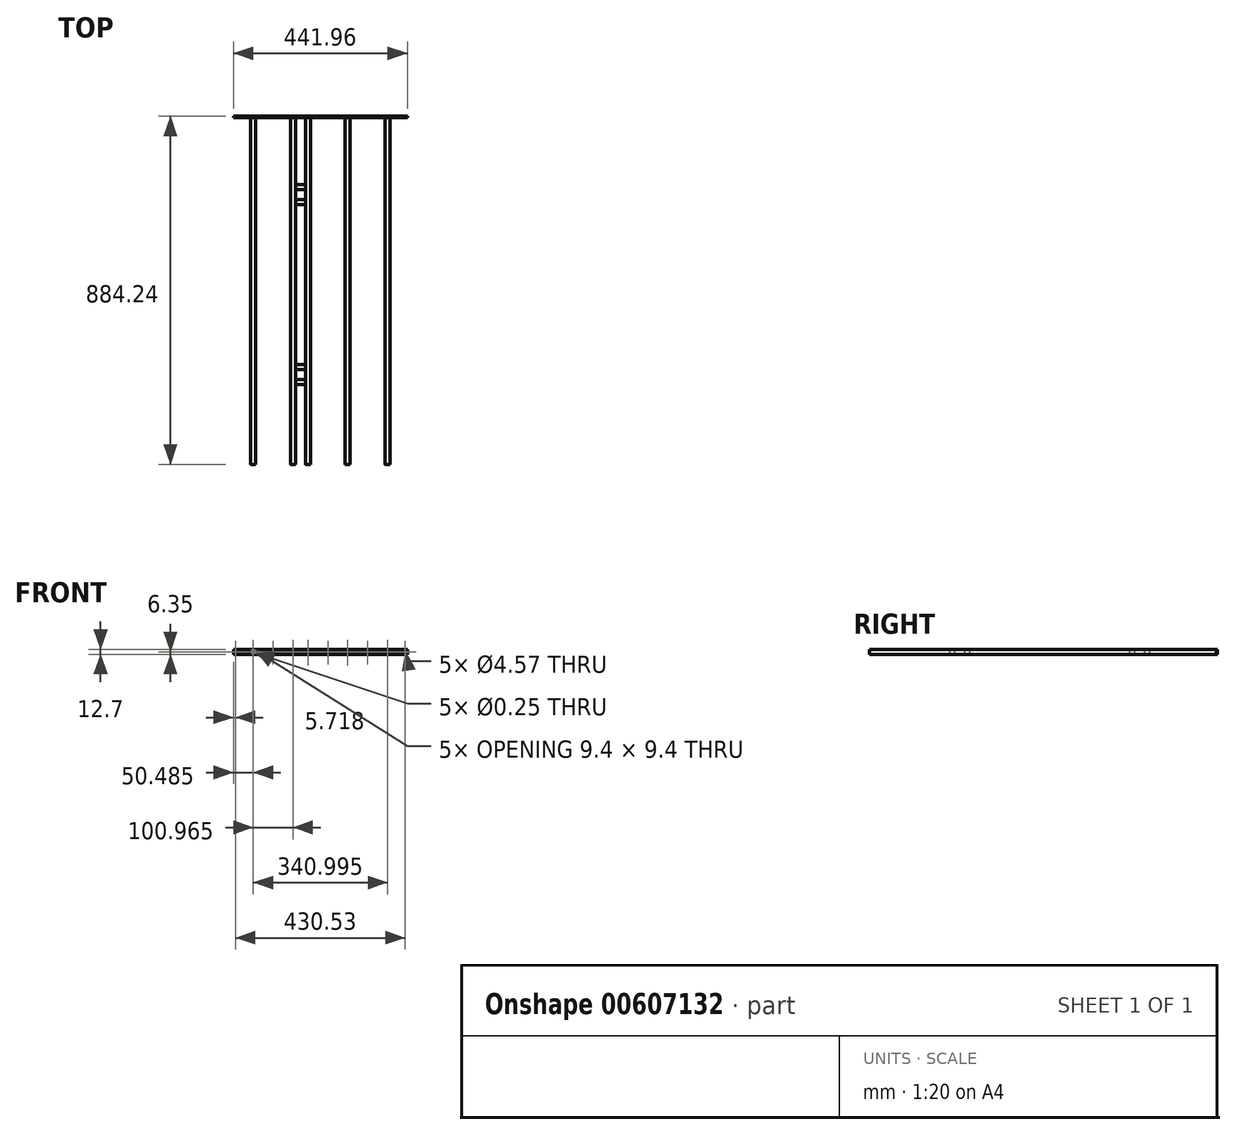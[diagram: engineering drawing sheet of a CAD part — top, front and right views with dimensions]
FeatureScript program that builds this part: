
annotation { "Feature Type Name" : "Feature", "Feature Type Description" : "" }
export const myFeature = defineFeature(function(context is Context, id is Id, definition is map)
    precondition{}
    {
        {
            var Q0;
            Q0=qCreatedBy(makeId("Front.planeOp"),FACE);
            var sketch = newSketch(context, id + "F0", { "sketchPlane" : qUnion([Q0])});
            skLineSegment(sketch, "E0.bottom", {"start": v(4.44, -6.35) * mm, "end": v(-4.44, -6.35) * mm});
            skLineSegment(sketch, "E0.top", {"start": v(4.45, 6.35) * mm, "end": v(-4.45, 6.35) * mm});
            skLineSegment(sketch, "E0.left", {"start": v(6.35, -4.45) * mm, "end": v(6.35, 4.45) * mm});
            skLineSegment(sketch, "E0.right", {"start": v(-6.35, -4.45) * mm, "end": v(-6.35, 4.45) * mm});
            skPoint(sketch, "E1.visualSharp", {"position": v(-6.35, 6.35) * mm});
            skArc(sketch, "E1.filletArc", {"start": v(-4.45, 6.35) * mm, "mid": v(-5.8, 5.8) * mm, "end": v(-6.35, 4.45) * mm});
            skPoint(sketch, "E2.visualSharp", {"position": v(6.35, 6.35) * mm});
            skArc(sketch, "E2.filletArc", {"start": v(6.35, 4.45) * mm, "mid": v(5.8, 5.8) * mm, "end": v(4.45, 6.35) * mm});
            skPoint(sketch, "E3.visualSharp", {"position": v(6.35, -6.35) * mm});
            skArc(sketch, "E3.filletArc", {"start": v(4.44, -6.35) * mm, "mid": v(5.8, -5.8) * mm, "end": v(6.35, -4.45) * mm});
            skPoint(sketch, "E4.visualSharp", {"position": v(-6.35, -6.35) * mm});
            skArc(sketch, "E4.filletArc", {"start": v(-6.35, -4.45) * mm, "mid": v(-5.8, -5.8) * mm, "end": v(-4.44, -6.35) * mm});
            skLineSegment(sketch, "E5", {"start": v(-6.35, 0) * mm, "end": v(6.35, 0) * mm, "construction": true});
            skLineSegment(sketch, "E6.0", {"start": v(4.45, 4.7) * mm, "end": v(-4.45, 4.7) * mm});
            skArc(sketch, "E7.0", {"start": v(4.7, 4.44) * mm, "mid": v(4.62, 4.62) * mm, "end": v(4.44, 4.7) * mm});
            skLineSegment(sketch, "E7.1", {"start": v(4.7, -4.44) * mm, "end": v(4.7, 4.44) * mm});
            skArc(sketch, "E7.2", {"start": v(4.44, -4.7) * mm, "mid": v(4.62, -4.62) * mm, "end": v(4.7, -4.44) * mm});
            skArc(sketch, "E7.3", {"start": v(-4.44, 4.7) * mm, "mid": v(-4.62, 4.62) * mm, "end": v(-4.7, 4.44) * mm});
            skLineSegment(sketch, "E7.4", {"start": v(-4.7, -4.44) * mm, "end": v(-4.7, 4.44) * mm});
            skArc(sketch, "E7.5", {"start": v(-4.7, -4.44) * mm, "mid": v(-4.62, -4.62) * mm, "end": v(-4.44, -4.7) * mm});
            skLineSegment(sketch, "E7.6", {"start": v(4.44, -4.7) * mm, "end": v(-4.44, -4.7) * mm});
            skLineSegment(sketch, "E8.1.0.0", {"start": v(33.4, -4.45) * mm, "end": v(33.4, 4.45) * mm});
            skLineSegment(sketch, "E8.1.0.1", {"start": v(42.55, -6.35) * mm, "end": v(33.66, -6.35) * mm});
            skLineSegment(sketch, "E8.1.0.2", {"start": v(44.45, -4.45) * mm, "end": v(44.45, 4.45) * mm});
            skLineSegment(sketch, "E8.1.0.3", {"start": v(42.55, -4.7) * mm, "end": v(33.66, -4.7) * mm});
            skLineSegment(sketch, "E8.1.0.4", {"start": v(31.75, 0) * mm, "end": v(44.45, 0) * mm, "construction": true});
            skPoint(sketch, "E8.1.0.5", {"position": v(44.45, 6.35) * mm});
            skLineSegment(sketch, "E8.1.0.6", {"start": v(42.55, 6.35) * mm, "end": v(33.66, 6.35) * mm});
            skPoint(sketch, "E8.1.0.7", {"position": v(31.75, -6.35) * mm});
            skLineSegment(sketch, "E8.1.0.8", {"start": v(31.75, -4.45) * mm, "end": v(31.75, 4.45) * mm});
            skPoint(sketch, "E8.1.0.9", {"position": v(31.75, 6.35) * mm});
            skLineSegment(sketch, "E8.1.0.10", {"start": v(42.55, 4.7) * mm, "end": v(33.66, 4.7) * mm});
            skLineSegment(sketch, "E8.1.0.11", {"start": v(42.8, -4.45) * mm, "end": v(42.8, 4.45) * mm});
            skPoint(sketch, "E8.1.0.12", {"position": v(44.45, -6.35) * mm});
            skArc(sketch, "E8.1.0.13", {"start": v(44.45, 4.45) * mm, "mid": v(43.9, 5.8) * mm, "end": v(42.55, 6.35) * mm});
            skArc(sketch, "E8.1.0.14", {"start": v(33.66, 6.35) * mm, "mid": v(32.3, 5.8) * mm, "end": v(31.75, 4.45) * mm});
            skArc(sketch, "E8.1.0.15", {"start": v(42.55, -6.35) * mm, "mid": v(43.9, -5.8) * mm, "end": v(44.45, -4.45) * mm});
            skArc(sketch, "E8.1.0.16", {"start": v(31.75, -4.45) * mm, "mid": v(32.3, -5.8) * mm, "end": v(33.66, -6.35) * mm});
            skArc(sketch, "E8.1.0.17", {"start": v(42.55, -4.7) * mm, "mid": v(42.72, -4.62) * mm, "end": v(42.8, -4.45) * mm});
            skArc(sketch, "E8.1.0.18", {"start": v(33.4, -4.45) * mm, "mid": v(33.48, -4.62) * mm, "end": v(33.66, -4.7) * mm});
            skArc(sketch, "E8.1.0.19", {"start": v(42.8, 4.45) * mm, "mid": v(42.72, 4.62) * mm, "end": v(42.55, 4.7) * mm});
            skArc(sketch, "E8.1.0.20", {"start": v(33.66, 4.7) * mm, "mid": v(33.48, 4.62) * mm, "end": v(33.4, 4.45) * mm});
            skLineSegment(sketch, "E8.direction1", {"start": v(-6.35, -6.35) * mm, "end": v(31.75, -6.35) * mm, "construction": true});
            skLineSegment(sketch, "E9.1.0.0", {"start": v(143.76, -4.44) * mm, "end": v(143.76, 4.45) * mm});
            skLineSegment(sketch, "E9.1.0.1", {"start": v(132.72, -4.44) * mm, "end": v(132.72, 4.45) * mm});
            skLineSegment(sketch, "E9.1.0.2", {"start": v(143.51, -4.7) * mm, "end": v(134.62, -4.7) * mm});
            skPoint(sketch, "E9.1.0.3", {"position": v(145.42, -6.35) * mm});
            skLineSegment(sketch, "E9.1.0.4", {"start": v(143.51, -6.35) * mm, "end": v(134.62, -6.35) * mm});
            skPoint(sketch, "E9.1.0.5", {"position": v(132.72, -6.35) * mm});
            skLineSegment(sketch, "E9.1.0.6", {"start": v(143.51, 4.7) * mm, "end": v(134.62, 4.7) * mm});
            skLineSegment(sketch, "E9.1.0.7", {"start": v(143.51, 6.35) * mm, "end": v(134.62, 6.35) * mm});
            skLineSegment(sketch, "E9.1.0.8", {"start": v(132.72, 0) * mm, "end": v(145.42, 0) * mm, "construction": true});
            skPoint(sketch, "E9.1.0.9", {"position": v(145.42, 6.35) * mm});
            skLineSegment(sketch, "E9.1.0.10", {"start": v(145.42, -4.44) * mm, "end": v(145.42, 4.45) * mm});
            skPoint(sketch, "E9.1.0.11", {"position": v(132.72, 6.35) * mm});
            skLineSegment(sketch, "E9.1.0.12", {"start": v(134.37, -4.44) * mm, "end": v(134.37, 4.45) * mm});
            skArc(sketch, "E9.1.0.13", {"start": v(134.62, 6.35) * mm, "mid": v(133.27, 5.8) * mm, "end": v(132.72, 4.45) * mm});
            skArc(sketch, "E9.1.0.14", {"start": v(132.72, -4.44) * mm, "mid": v(133.27, -5.8) * mm, "end": v(134.62, -6.35) * mm});
            skArc(sketch, "E9.1.0.15", {"start": v(143.51, -6.35) * mm, "mid": v(144.86, -5.8) * mm, "end": v(145.42, -4.44) * mm});
            skArc(sketch, "E9.1.0.16", {"start": v(143.76, 4.45) * mm, "mid": v(143.69, 4.62) * mm, "end": v(143.51, 4.7) * mm});
            skArc(sketch, "E9.1.0.17", {"start": v(145.42, 4.45) * mm, "mid": v(144.86, 5.8) * mm, "end": v(143.51, 6.35) * mm});
            skArc(sketch, "E9.1.0.18", {"start": v(134.37, -4.44) * mm, "mid": v(134.44, -4.62) * mm, "end": v(134.62, -4.7) * mm});
            skArc(sketch, "E9.1.0.19", {"start": v(134.62, 4.7) * mm, "mid": v(134.44, 4.62) * mm, "end": v(134.37, 4.45) * mm});
            skArc(sketch, "E9.1.0.20", {"start": v(143.51, -4.7) * mm, "mid": v(143.69, -4.62) * mm, "end": v(143.76, -4.44) * mm});
            skLineSegment(sketch, "E9.direction1", {"start": v(31.75, -6.35) * mm, "end": v(132.72, -6.35) * mm, "construction": true});
            skLineSegment(sketch, "E10.0.2.0", {"start": v(244.73, -4.44) * mm, "end": v(244.73, 4.45) * mm});
            skLineSegment(sketch, "E10.3.2.0", {"start": v(233.68, -4.44) * mm, "end": v(233.68, 4.45) * mm});
            skLineSegment(sketch, "E10.6.2.0", {"start": v(244.48, -4.7) * mm, "end": v(235.59, -4.7) * mm});
            skPoint(sketch, "E10.9.2.0", {"position": v(246.38, -6.35) * mm});
            skLineSegment(sketch, "E10.10.2.0", {"start": v(244.48, -6.35) * mm, "end": v(235.59, -6.35) * mm});
            skPoint(sketch, "E10.13.2.0", {"position": v(233.68, -6.35) * mm});
            skLineSegment(sketch, "E10.14.2.0", {"start": v(244.48, 4.7) * mm, "end": v(235.59, 4.7) * mm});
            skLineSegment(sketch, "E10.17.2.0", {"start": v(244.48, 6.35) * mm, "end": v(235.59, 6.35) * mm});
            skLineSegment(sketch, "E10.20.2.0", {"start": v(233.68, 0) * mm, "end": v(246.38, 0) * mm, "construction": true});
            skPoint(sketch, "E10.23.2.0", {"position": v(246.38, 6.35) * mm});
            skLineSegment(sketch, "E10.24.2.0", {"start": v(246.38, -4.44) * mm, "end": v(246.38, 4.45) * mm});
            skPoint(sketch, "E10.27.2.0", {"position": v(233.68, 6.35) * mm});
            skLineSegment(sketch, "E10.28.2.0", {"start": v(235.33, -4.44) * mm, "end": v(235.33, 4.45) * mm});
            skArc(sketch, "E10.31.2.0", {"start": v(235.59, 6.35) * mm, "mid": v(234.24, 5.8) * mm, "end": v(233.68, 4.45) * mm});
            skArc(sketch, "E10.35.2.0", {"start": v(233.68, -4.44) * mm, "mid": v(234.24, -5.8) * mm, "end": v(235.59, -6.35) * mm});
            skArc(sketch, "E10.39.2.0", {"start": v(244.48, -6.35) * mm, "mid": v(245.82, -5.8) * mm, "end": v(246.38, -4.44) * mm});
            skArc(sketch, "E10.43.2.0", {"start": v(244.73, 4.45) * mm, "mid": v(244.65, 4.62) * mm, "end": v(244.48, 4.7) * mm});
            skArc(sketch, "E10.47.2.0", {"start": v(246.38, 4.45) * mm, "mid": v(245.82, 5.8) * mm, "end": v(244.48, 6.35) * mm});
            skArc(sketch, "E10.51.2.0", {"start": v(235.33, -4.44) * mm, "mid": v(235.4, -4.62) * mm, "end": v(235.59, -4.7) * mm});
            skArc(sketch, "E10.55.2.0", {"start": v(235.59, 4.7) * mm, "mid": v(235.4, 4.62) * mm, "end": v(235.33, 4.45) * mm});
            skArc(sketch, "E10.59.2.0", {"start": v(244.48, -4.7) * mm, "mid": v(244.65, -4.62) * mm, "end": v(244.73, -4.44) * mm});
            skPoint(sketch, "E11.1.0.0", {"position": v(-107.32, 6.35) * mm});
            skPoint(sketch, "E11.1.0.1", {"position": v(-94.62, -6.35) * mm});
            skLineSegment(sketch, "E11.1.0.2", {"start": v(-96.52, -4.7) * mm, "end": v(-105.41, -4.7) * mm});
            skPoint(sketch, "E11.1.0.3", {"position": v(-107.32, -6.35) * mm});
            skLineSegment(sketch, "E11.1.0.4", {"start": v(-96.52, -6.35) * mm, "end": v(-105.41, -6.35) * mm});
            skLineSegment(sketch, "E11.1.0.5", {"start": v(-96.27, -4.45) * mm, "end": v(-96.27, 4.45) * mm});
            skLineSegment(sketch, "E11.1.0.6", {"start": v(-107.32, 0) * mm, "end": v(-94.62, 0) * mm, "construction": true});
            skPoint(sketch, "E11.1.0.7", {"position": v(-94.62, 6.35) * mm});
            skLineSegment(sketch, "E11.1.0.8", {"start": v(-94.62, -4.45) * mm, "end": v(-94.62, 4.45) * mm});
            skLineSegment(sketch, "E11.1.0.9", {"start": v(-96.52, 6.35) * mm, "end": v(-105.41, 6.35) * mm});
            skLineSegment(sketch, "E11.1.0.10", {"start": v(-105.66, -4.45) * mm, "end": v(-105.66, 4.45) * mm});
            skLineSegment(sketch, "E11.1.0.11", {"start": v(-96.52, 4.7) * mm, "end": v(-105.41, 4.7) * mm});
            skLineSegment(sketch, "E11.1.0.12", {"start": v(-107.32, -4.45) * mm, "end": v(-107.32, 4.45) * mm});
            skArc(sketch, "E11.1.0.13", {"start": v(-94.62, 4.45) * mm, "mid": v(-95.17, 5.8) * mm, "end": v(-96.52, 6.35) * mm});
            skArc(sketch, "E11.1.0.14", {"start": v(-96.27, 4.45) * mm, "mid": v(-96.34, 4.62) * mm, "end": v(-96.52, 4.7) * mm});
            skArc(sketch, "E11.1.0.15", {"start": v(-105.41, 4.7) * mm, "mid": v(-105.59, 4.62) * mm, "end": v(-105.66, 4.45) * mm});
            skArc(sketch, "E11.1.0.16", {"start": v(-105.41, 6.35) * mm, "mid": v(-106.76, 5.8) * mm, "end": v(-107.32, 4.45) * mm});
            skArc(sketch, "E11.1.0.17", {"start": v(-107.32, -4.45) * mm, "mid": v(-106.76, -5.8) * mm, "end": v(-105.41, -6.35) * mm});
            skArc(sketch, "E11.1.0.18", {"start": v(-105.66, -4.45) * mm, "mid": v(-105.59, -4.62) * mm, "end": v(-105.41, -4.7) * mm});
            skArc(sketch, "E11.1.0.19", {"start": v(-96.52, -6.35) * mm, "mid": v(-95.17, -5.8) * mm, "end": v(-94.62, -4.45) * mm});
            skArc(sketch, "E11.1.0.20", {"start": v(-96.52, -4.7) * mm, "mid": v(-96.34, -4.62) * mm, "end": v(-96.27, -4.45) * mm});
            skLineSegment(sketch, "E11.direction1", {"start": v(-6.35, -6.35) * mm, "end": v(-107.32, -6.35) * mm, "construction": true});
            skSolve(sketch);
        }
        {
            var Q0;
            Q0=makeQuery(id+"F0.imprint","IMPRINT",FACE,{"disambiguationData":[TD([[makeQuery(id+"F0.imprint","IMPRINT",EDGE,{"derivedFrom":sQuery(id+"F0.wireOp",EDGE,"E0.bottom")}),-1.0]])]});
            var Q1;
            Q1=makeQuery(id+"F0.imprint","IMPRINT",FACE,{"disambiguationData":[TD([[makeQuery(id+"F0.imprint","IMPRINT",EDGE,{"derivedFrom":sQuery(id+"F0.wireOp",EDGE,"E8.1.0.0")}),1.0]])]});
            var Q2;
            Q2=makeQuery(id+"F0.imprint","IMPRINT",FACE,{"disambiguationData":[TD([[makeQuery(id+"F0.imprint","IMPRINT",EDGE,{"derivedFrom":sQuery(id+"F0.wireOp",EDGE,"E9.1.0.0")}),-1.0]])]});
            var Q3;
            Q3=makeQuery(id+"F0.imprint","IMPRINT",FACE,{"disambiguationData":[TD([[makeQuery(id+"F0.imprint","IMPRINT",EDGE,{"derivedFrom":sQuery(id+"F0.wireOp",EDGE,"E10.0.2.0")}),-1.0]])]});
            var Q4;
            Q4=makeQuery(id+"F0.imprint","IMPRINT",FACE,{"disambiguationData":[TD([[makeQuery(id+"F0.imprint","IMPRINT",EDGE,{"derivedFrom":sQuery(id+"F0.wireOp",EDGE,"E11.1.0.2")}),1.0]])]});
            extrude(context, id + "F1", {"entities" : qUnion([Q0, Q1, Q2, Q3, Q4]), "depth" : 881.06 * mm, "offsetDistance" : 25.4 * mm});
        }
        {
            var Q0;
            Q0=makeQuery(id+"F1.opExtrude","SWEPT_FACE",FACE,{"disambiguationData":[OSD([sQuery(id+"F0.wireOp",EDGE,"E0.left")])]});
            var sketch = newSketch(context, id + "F2", { "sketchPlane" : qUnion([Q0])});
            skLineSegment(sketch, "E12.bottom", {"start": v(-667.07, 6.35) * mm, "end": v(-675.96, 6.35) * mm});
            skLineSegment(sketch, "E12.top", {"start": v(-667.07, -6.35) * mm, "end": v(-675.96, -6.35) * mm});
            skLineSegment(sketch, "E12.left", {"start": v(-665.16, 4.45) * mm, "end": v(-665.16, -4.44) * mm});
            skLineSegment(sketch, "E12.right", {"start": v(-677.86, 4.45) * mm, "end": v(-677.86, -4.44) * mm});
            skPoint(sketch, "E13.visualSharp", {"position": v(-665.16, -6.35) * mm});
            skArc(sketch, "E13.filletArc", {"start": v(-667.07, -6.35) * mm, "mid": v(-665.72, -5.8) * mm, "end": v(-665.16, -4.44) * mm});
            skPoint(sketch, "E14.visualSharp", {"position": v(-677.86, -6.35) * mm});
            skArc(sketch, "E14.filletArc", {"start": v(-677.86, -4.44) * mm, "mid": v(-677.3, -5.8) * mm, "end": v(-675.96, -6.35) * mm});
            skPoint(sketch, "E15.visualSharp", {"position": v(-677.86, 6.35) * mm});
            skArc(sketch, "E15.filletArc", {"start": v(-675.96, 6.35) * mm, "mid": v(-677.3, 5.8) * mm, "end": v(-677.86, 4.45) * mm});
            skPoint(sketch, "E16.visualSharp", {"position": v(-665.16, 6.35) * mm});
            skArc(sketch, "E16.filletArc", {"start": v(-665.16, 4.45) * mm, "mid": v(-665.72, 5.8) * mm, "end": v(-667.07, 6.35) * mm});
            skPoint(sketch, "E17.1.0.0", {"position": v(-627.06, 6.35) * mm});
            skPoint(sketch, "E17.1.0.1", {"position": v(-639.76, 6.35) * mm});
            skPoint(sketch, "E17.1.0.2", {"position": v(-639.76, -6.35) * mm});
            skPoint(sketch, "E17.1.0.3", {"position": v(-627.06, -6.35) * mm});
            skLineSegment(sketch, "E17.1.0.4", {"start": v(-628.97, 6.35) * mm, "end": v(-637.86, 6.35) * mm});
            skLineSegment(sketch, "E17.1.0.5", {"start": v(-628.97, -6.35) * mm, "end": v(-637.86, -6.35) * mm});
            skLineSegment(sketch, "E17.1.0.6", {"start": v(-627.06, 4.45) * mm, "end": v(-627.06, -4.44) * mm});
            skLineSegment(sketch, "E17.1.0.7", {"start": v(-639.76, 4.45) * mm, "end": v(-639.76, -4.44) * mm});
            skArc(sketch, "E17.1.0.8", {"start": v(-628.97, -6.35) * mm, "mid": v(-627.62, -5.8) * mm, "end": v(-627.06, -4.44) * mm});
            skArc(sketch, "E17.1.0.9", {"start": v(-627.06, 4.45) * mm, "mid": v(-627.62, 5.8) * mm, "end": v(-628.97, 6.35) * mm});
            skArc(sketch, "E17.1.0.10", {"start": v(-639.76, -4.44) * mm, "mid": v(-639.2, -5.8) * mm, "end": v(-637.86, -6.35) * mm});
            skArc(sketch, "E17.1.0.11", {"start": v(-637.86, 6.35) * mm, "mid": v(-639.2, 5.8) * mm, "end": v(-639.76, 4.45) * mm});
            skLineSegment(sketch, "E17.direction1", {"start": v(-677.86, -6.35) * mm, "end": v(-639.76, -6.35) * mm, "construction": true});
            skPoint(sketch, "E18.1.0.0", {"position": v(-182.56, 6.35) * mm});
            skLineSegment(sketch, "E18.1.0.1", {"start": v(-220.66, -6.35) * mm, "end": v(-182.56, -6.35) * mm, "construction": true});
            skLineSegment(sketch, "E18.1.0.2", {"start": v(-171.77, -6.35) * mm, "end": v(-180.66, -6.35) * mm});
            skLineSegment(sketch, "E18.1.0.3", {"start": v(-171.77, 6.35) * mm, "end": v(-180.66, 6.35) * mm});
            skPoint(sketch, "E18.1.0.4", {"position": v(-182.56, -6.35) * mm});
            skPoint(sketch, "E18.1.0.5", {"position": v(-169.86, 6.35) * mm});
            skPoint(sketch, "E18.1.0.6", {"position": v(-207.96, 6.35) * mm});
            skPoint(sketch, "E18.1.0.7", {"position": v(-220.66, 6.35) * mm});
            skPoint(sketch, "E18.1.0.8", {"position": v(-169.86, -6.35) * mm});
            skPoint(sketch, "E18.1.0.9", {"position": v(-220.66, -6.35) * mm});
            skPoint(sketch, "E18.1.0.10", {"position": v(-207.96, -6.35) * mm});
            skLineSegment(sketch, "E18.1.0.11", {"start": v(-209.87, 6.35) * mm, "end": v(-218.76, 6.35) * mm});
            skLineSegment(sketch, "E18.1.0.12", {"start": v(-207.96, 4.45) * mm, "end": v(-207.96, -4.44) * mm});
            skArc(sketch, "E18.1.0.13", {"start": v(-171.77, -6.35) * mm, "mid": v(-170.42, -5.8) * mm, "end": v(-169.86, -4.44) * mm});
            skLineSegment(sketch, "E18.1.0.14", {"start": v(-182.56, 4.45) * mm, "end": v(-182.56, -4.44) * mm});
            skLineSegment(sketch, "E18.1.0.15", {"start": v(-169.86, 4.45) * mm, "end": v(-169.86, -4.44) * mm});
            skArc(sketch, "E18.1.0.16", {"start": v(-182.56, -4.44) * mm, "mid": v(-182, -5.8) * mm, "end": v(-180.66, -6.35) * mm});
            skLineSegment(sketch, "E18.1.0.17", {"start": v(-209.87, -6.35) * mm, "end": v(-218.76, -6.35) * mm});
            skLineSegment(sketch, "E18.1.0.18", {"start": v(-220.66, 4.45) * mm, "end": v(-220.66, -4.44) * mm});
            skArc(sketch, "E18.1.0.19", {"start": v(-218.76, 6.35) * mm, "mid": v(-220.1, 5.8) * mm, "end": v(-220.66, 4.45) * mm});
            skArc(sketch, "E18.1.0.20", {"start": v(-207.96, 4.45) * mm, "mid": v(-208.52, 5.8) * mm, "end": v(-209.87, 6.35) * mm});
            skArc(sketch, "E18.1.0.21", {"start": v(-169.86, 4.45) * mm, "mid": v(-170.42, 5.8) * mm, "end": v(-171.77, 6.35) * mm});
            skArc(sketch, "E18.1.0.22", {"start": v(-180.66, 6.35) * mm, "mid": v(-182, 5.8) * mm, "end": v(-182.56, 4.45) * mm});
            skArc(sketch, "E18.1.0.23", {"start": v(-209.87, -6.35) * mm, "mid": v(-208.52, -5.8) * mm, "end": v(-207.96, -4.44) * mm});
            skArc(sketch, "E18.1.0.24", {"start": v(-220.66, -4.44) * mm, "mid": v(-220.1, -5.8) * mm, "end": v(-218.76, -6.35) * mm});
            skLineSegment(sketch, "E18.direction1", {"start": v(-677.86, -6.35) * mm, "end": v(-220.66, -6.35) * mm, "construction": true});
            skSolve(sketch);
        }
        {
            var Q0;
            Q0 = qSketchRegion(id + "F2", true);
            extrude(context, id + "F3", {"entities" : qUnion([Q0]), "depth" : 25.4 * mm, "offsetDistance" : 25.4 * mm});
        }
        {
            var Q0;
            Q0=qCreatedBy(makeId("Front.planeOp"),FACE);
            var sketch = newSketch(context, id + "F4", { "sketchPlane" : qUnion([Q0])});
            skLineSegment(sketch, "E19.bottom", {"start": v(290.51, -6.35) * mm, "end": v(-151.45, -6.35) * mm});
            skLineSegment(sketch, "E19.top", {"start": v(290.51, 6.35) * mm, "end": v(-151.45, 6.35) * mm});
            skLineSegment(sketch, "E19.left", {"start": v(290.51, -6.35) * mm, "end": v(290.51, 6.35) * mm});
            skLineSegment(sketch, "E19.right", {"start": v(-151.45, -6.35) * mm, "end": v(-151.45, 6.35) * mm});
            skCircle(sketch, "E20", {"center": v(-50.48, 0) * mm, "radius": 2.29 * mm});
            skCircle(sketch, "E21", {"center": v(-145.73, 0) * mm, "radius": 2.29 * mm});
            skCircle(sketch, "E22", {"center": v(88.58, 0) * mm, "radius": 2.29 * mm});
            skCircle(sketch, "E23", {"center": v(189.55, 0) * mm, "radius": 2.29 * mm});
            skCircle(sketch, "E24", {"center": v(284.8, 0) * mm, "radius": 2.29 * mm});
            skCircle(sketch, "E25", {"center": v(139.06, 0) * mm, "radius": 0.13 * mm});
            skCircle(sketch, "E26", {"center": v(240.03, 0) * mm, "radius": 0.13 * mm});
            skCircle(sketch, "E27", {"center": v(38.1, 0) * mm, "radius": 0.13 * mm});
            skCircle(sketch, "E28", {"center": v(0, 0) * mm, "radius": 0.13 * mm});
            skCircle(sketch, "E29", {"center": v(-100.97, 0) * mm, "radius": 0.13 * mm});
            skSolve(sketch);
        }
        {
            var Q0;
            Q0 = qSketchRegion(id + "F4", true);
            extrude(context, id + "F5", {"entities" : qUnion([Q0]), "oppositeDirection" : true, "depth" : 3.17 * mm, "offsetDistance" : 25.4 * mm});
        }
    });
